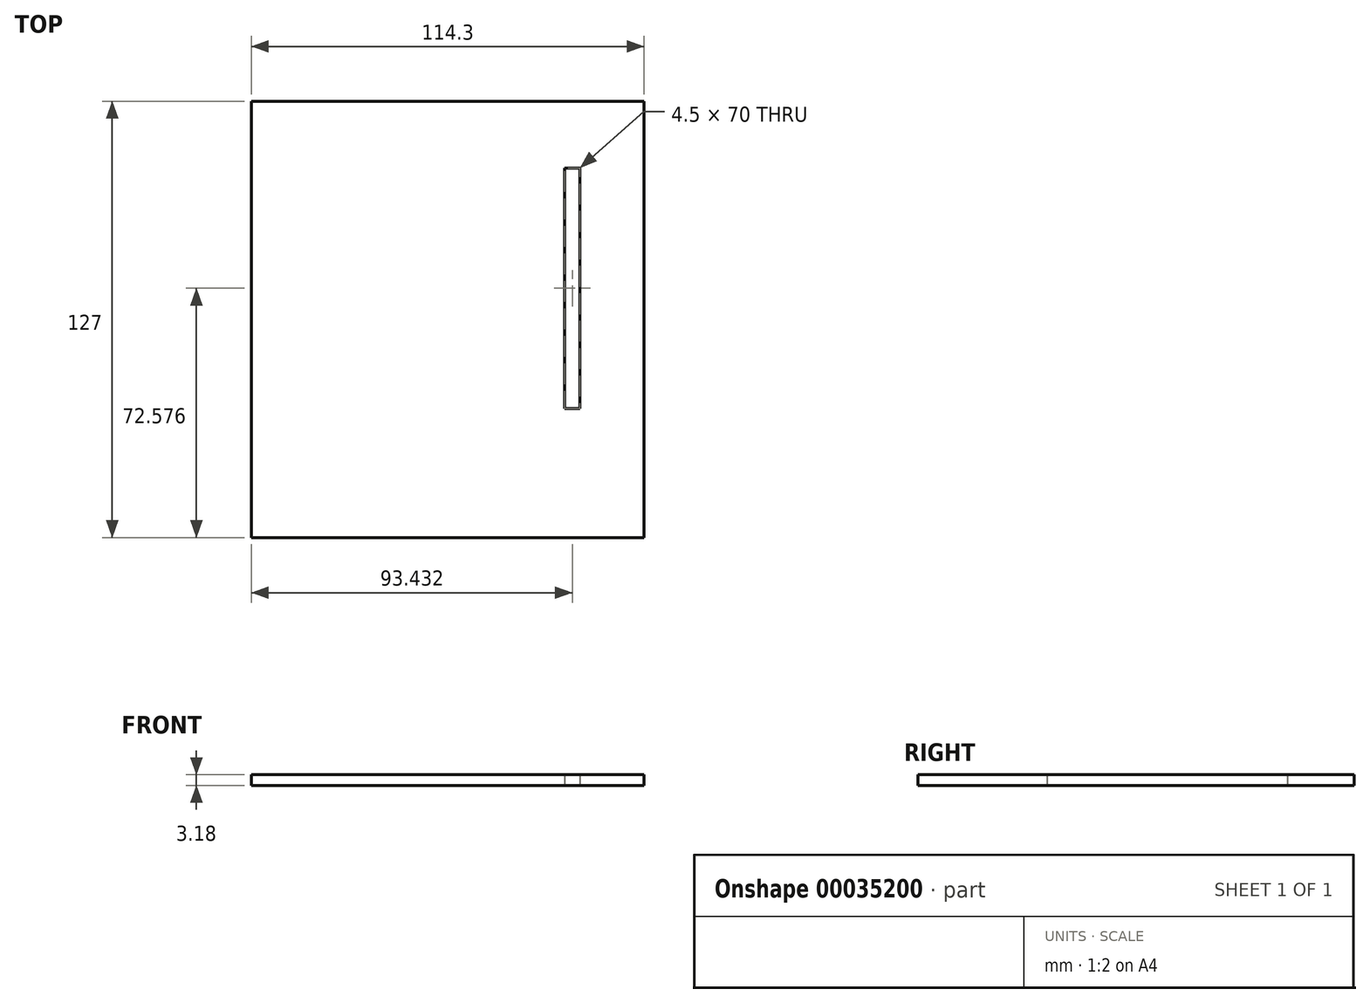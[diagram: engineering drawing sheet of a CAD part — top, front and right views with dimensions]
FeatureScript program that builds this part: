
annotation { "Feature Type Name" : "Feature", "Feature Type Description" : "" }
export const myFeature = defineFeature(function(context is Context, id is Id, definition is map)
    precondition{}
    {
        {
            var Q0;
            Q0=qCreatedBy(makeId("Top.planeOp"),FACE);
            var sketch = newSketch(context, id + "F0", { "sketchPlane" : qUnion([Q0])});
            skLineSegment(sketch, "E0.bottom", {"start": v(-58.4, 69.55) * mm, "end": v(55.9, 69.55) * mm});
            skLineSegment(sketch, "E0.top", {"start": v(-58.4, -57.45) * mm, "end": v(55.9, -57.45) * mm});
            skLineSegment(sketch, "E0.left", {"start": v(-58.4, 69.55) * mm, "end": v(-58.4, -57.45) * mm});
            skLineSegment(sketch, "E0.right", {"start": v(55.9, 69.55) * mm, "end": v(55.9, -57.45) * mm});
            skLineSegment(sketch, "E1.bottom", {"start": v(32.8, 50.13) * mm, "end": v(37.3, 50.13) * mm});
            skLineSegment(sketch, "E1.top", {"start": v(32.8, -19.87) * mm, "end": v(37.3, -19.87) * mm});
            skLineSegment(sketch, "E1.left", {"start": v(32.8, 50.13) * mm, "end": v(32.8, -19.87) * mm});
            skLineSegment(sketch, "E1.right", {"start": v(37.3, 50.13) * mm, "end": v(37.3, -19.87) * mm});
            skSolve(sketch);
        }
        {
            var Q0;
            Q0=makeQuery(id+"F0.imprint","IMPRINT",FACE,{"disambiguationData":[TD([[makeQuery(id+"F0.imprint","IMPRINT",EDGE,{"derivedFrom":sQuery(id+"F0.wireOp",EDGE,"E0.bottom")}),-1.0]])]});
            extrude(context, id + "F1", {"entities" : qUnion([Q0]), "depth" : 3.18 * mm});
        }
    });
